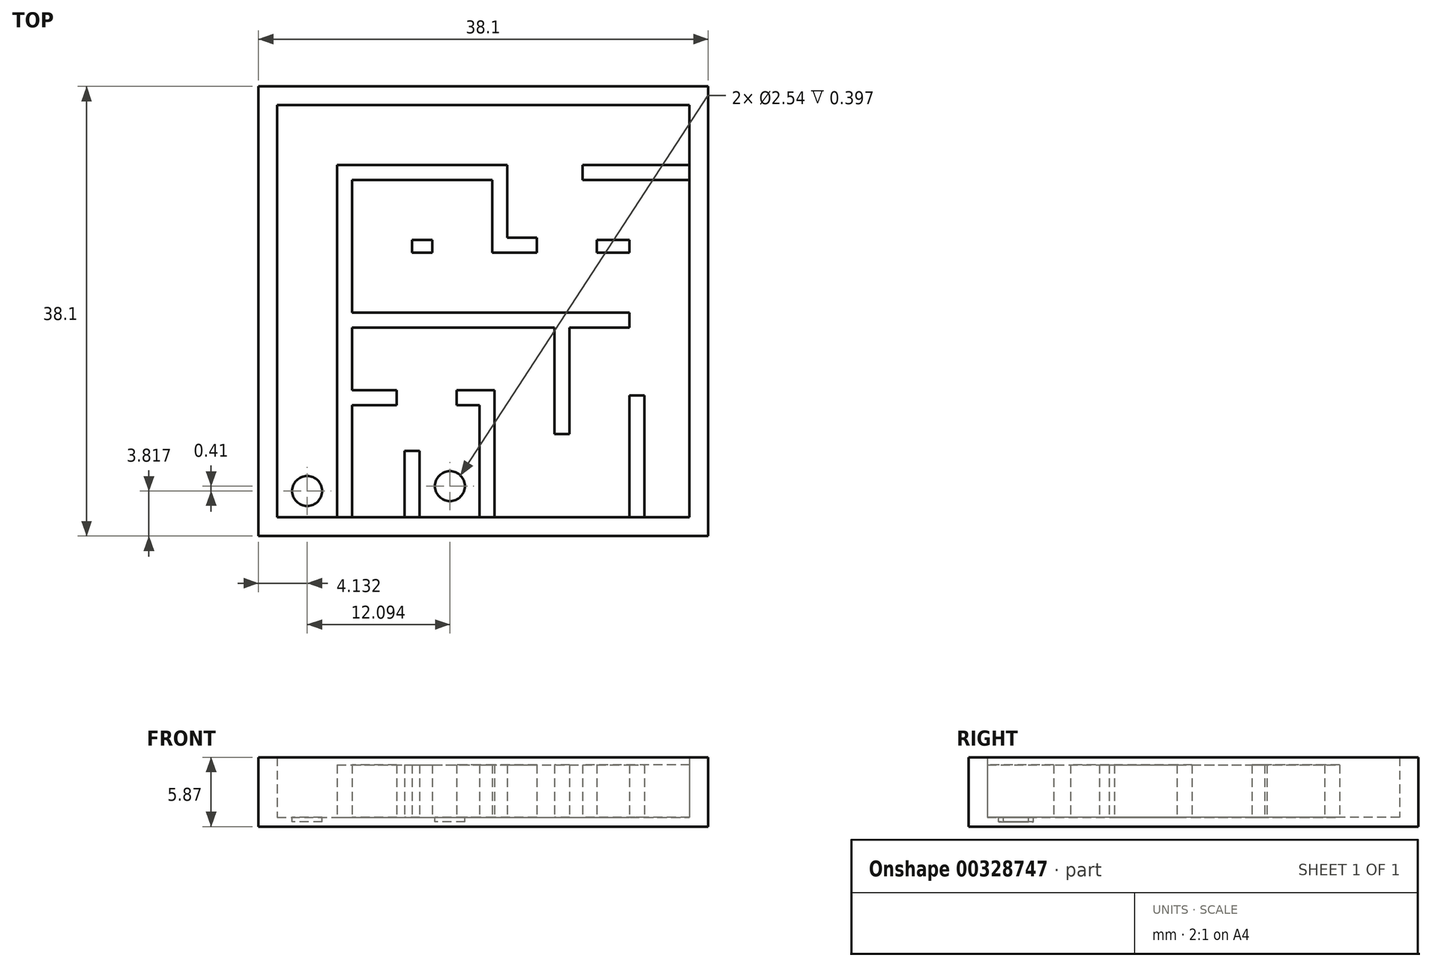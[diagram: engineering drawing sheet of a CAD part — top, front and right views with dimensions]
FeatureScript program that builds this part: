
annotation { "Feature Type Name" : "Feature", "Feature Type Description" : "" }
export const myFeature = defineFeature(function(context is Context, id is Id, definition is map)
    precondition{}
    {
        {
            var Q0;
            Q0=qCreatedBy(makeId("Top.planeOp"),FACE);
            var sketch = newSketch(context, id + "F0", { "sketchPlane" : qUnion([Q0])});
            skLineSegment(sketch, "E0.bottom", {"start": v(-18.59, 18.21) * mm, "end": v(19.51, 18.21) * mm});
            skLineSegment(sketch, "E0.top", {"start": v(-18.59, -19.89) * mm, "end": v(19.51, -19.89) * mm});
            skLineSegment(sketch, "E0.left", {"start": v(-18.59, 18.21) * mm, "end": v(-18.59, -19.89) * mm});
            skLineSegment(sketch, "E0.right", {"start": v(19.51, 18.21) * mm, "end": v(19.51, -19.89) * mm});
            skSolve(sketch);
        }
        {
            var Q0;
            Q0=makeQuery(id+"F0.imprint","IMPRINT",FACE,{"disambiguationData":[TD([[makeQuery(id+"F0.imprint","IMPRINT",EDGE,{"derivedFrom":sQuery(id+"F0.wireOp",EDGE,"E0.bottom")}),-1.0]])]});
            extrude(context, id + "F1", {"entities" : qUnion([Q0]), "depth" : 0.8 * mm});
        }
        {
            var Q0;
            Q0=makeQuery(id+"F1.opExtrude","CAP_FACE",FACE,{"disambiguationData":[OSD([sQuery(id+"F0.wireOp",EDGE,"E0.bottom"),sQuery(id+"F0.wireOp",EDGE,"E0.top"),sQuery(id+"F0.wireOp",EDGE,"E0.left"),sQuery(id+"F0.wireOp",EDGE,"E0.right")])],"isStart":false});
            var sketch = newSketch(context, id + "F2", { "sketchPlane" : qUnion([Q0])});
            skLineSegment(sketch, "E1.0", {"start": v(-17, 16.62) * mm, "end": v(17.93, 16.62) * mm});
            skLineSegment(sketch, "E1.1", {"start": v(-17, 16.62) * mm, "end": v(-17, -18.3) * mm});
            skLineSegment(sketch, "E1.2", {"start": v(-17, -18.3) * mm, "end": v(17.93, -18.3) * mm});
            skLineSegment(sketch, "E1.3", {"start": v(17.93, 16.62) * mm, "end": v(17.93, -18.3) * mm});
            skSolve(sketch);
        }
        {
            var Q0;
            Q0=makeQuery(id+"F2.imprint","IMPRINT",FACE,{"disambiguationData":[TD([[makeQuery(id+"F2.imprint","IMPRINT",EDGE,{"derivedFrom":sQuery(id+"F2.wireOp",EDGE,"E1.0")}),1.0]])]});
            extrude(context, id + "F3", {"entities" : qUnion([Q0]), "operationType" : NewBodyOperationType.ADD, "depth" : 5.08 * mm});
        }
        {
            var Q0;
            Q0=makeQuery(id+"F1.opExtrude","CAP_FACE",FACE,{"disambiguationData":[OSD([sQuery(id+"F0.wireOp",EDGE,"E0.bottom"),sQuery(id+"F0.wireOp",EDGE,"E0.top"),sQuery(id+"F0.wireOp",EDGE,"E0.left"),sQuery(id+"F0.wireOp",EDGE,"E0.right")])],"isStart":false});
            var sketch = newSketch(context, id + "F4", { "sketchPlane" : qUnion([Q0])});
            skLineSegment(sketch, "E2.bottom", {"start": v(-11.92, -18.3) * mm, "end": v(-10.65, -18.3) * mm});
            skLineSegment(sketch, "E2.top", {"start": v(-11.92, 11.54) * mm, "end": v(-10.65, 11.54) * mm});
            skLineSegment(sketch, "E2.left", {"start": v(-11.92, -18.3) * mm, "end": v(-11.92, 11.54) * mm});
            skLineSegment(sketch, "E2.right", {"start": v(-10.65, -18.3) * mm, "end": v(-10.65, -8.81) * mm});
            skLineSegment(sketch, "E3.bottom", {"start": v(-10.65, 11.54) * mm, "end": v(2.5, 11.54) * mm});
            skLineSegment(sketch, "E3.top", {"start": v(-10.65, 10.27) * mm, "end": v(1.22, 10.27) * mm});
            skLineSegment(sketch, "E3.right", {"start": v(2.5, 11.54) * mm, "end": v(2.5, 10.27) * mm});
            skLineSegment(sketch, "E4.bottom", {"start": v(17.93, 11.54) * mm, "end": v(8.87, 11.54) * mm});
            skLineSegment(sketch, "E4.top", {"start": v(17.93, 10.27) * mm, "end": v(8.87, 10.27) * mm});
            skLineSegment(sketch, "E4.left", {"start": v(17.93, 11.54) * mm, "end": v(17.93, 10.27) * mm});
            skLineSegment(sketch, "E4.right", {"start": v(8.87, 11.54) * mm, "end": v(8.87, 10.27) * mm});
            skLineSegment(sketch, "E5.top", {"start": v(2.5, 4.12) * mm, "end": v(1.22, 4.12) * mm});
            skLineSegment(sketch, "E5.left", {"start": v(2.5, 10.27) * mm, "end": v(2.5, 5.4) * mm});
            skLineSegment(sketch, "E5.right", {"start": v(1.22, 10.27) * mm, "end": v(1.22, 4.12) * mm});
            skLineSegment(sketch, "E6.bottom", {"start": v(-10.65, -0.96) * mm, "end": v(12.85, -0.96) * mm});
            skLineSegment(sketch, "E6.top", {"start": v(-10.65, -2.23) * mm, "end": v(6.5, -2.23) * mm});
            skLineSegment(sketch, "E6.right", {"start": v(12.85, -0.96) * mm, "end": v(12.85, -2.23) * mm});
            skLineSegment(sketch, "E7.trimOffspring", {"start": v(-10.65, -0.96) * mm, "end": v(-10.65, 10.27) * mm});
            skLineSegment(sketch, "E8.bottom", {"start": v(2.5, 4.12) * mm, "end": v(5, 4.12) * mm});
            skLineSegment(sketch, "E8.top", {"start": v(2.5, 5.4) * mm, "end": v(5, 5.4) * mm});
            skLineSegment(sketch, "E8.right", {"start": v(5, 4.12) * mm, "end": v(5, 5.4) * mm});
            skLineSegment(sketch, "E9.bottom", {"start": v(14.12, -18.3) * mm, "end": v(12.85, -18.3) * mm});
            skLineSegment(sketch, "E9.top", {"start": v(14.12, -8) * mm, "end": v(12.85, -8) * mm});
            skLineSegment(sketch, "E9.left", {"start": v(14.12, -18.3) * mm, "end": v(14.12, -8) * mm});
            skLineSegment(sketch, "E9.right", {"start": v(12.85, -18.3) * mm, "end": v(12.85, -8) * mm});
            skLineSegment(sketch, "E10", {"start": v(-11.92, -18.3) * mm, "end": v(-17, -18.3) * mm});
            skCircle(sketch, "E11", {"center": v(-14.46, -16.07) * mm, "radius": 1.27 * mm});
            skPoint(sketch, "E11.centerSnap0", {"position": v(-14.46, -18.3) * mm});
            skLineSegment(sketch, "E12.bottom", {"start": v(10.08, 5.2) * mm, "end": v(12.85, 5.2) * mm});
            skLineSegment(sketch, "E12.top", {"start": v(10.08, 4.12) * mm, "end": v(12.85, 4.12) * mm});
            skLineSegment(sketch, "E12.left", {"start": v(10.08, 5.2) * mm, "end": v(10.08, 4.12) * mm});
            skLineSegment(sketch, "E12.right", {"start": v(12.85, 5.2) * mm, "end": v(12.85, 4.12) * mm});
            skLineSegment(sketch, "E13.top", {"start": v(7.77, -11.26) * mm, "end": v(6.5, -11.26) * mm});
            skLineSegment(sketch, "E13.left", {"start": v(7.77, -2.23) * mm, "end": v(7.77, -11.26) * mm});
            skLineSegment(sketch, "E13.right", {"start": v(6.5, -2.23) * mm, "end": v(6.5, -11.26) * mm});
            skLineSegment(sketch, "E14.bottom", {"start": v(1.42, -18.3) * mm, "end": v(0.15, -18.3) * mm});
            skLineSegment(sketch, "E14.top", {"start": v(1.42, -7.54) * mm, "end": v(0.15, -7.54) * mm});
            skLineSegment(sketch, "E14.left", {"start": v(0.15, -18.3) * mm, "end": v(0.15, -8.81) * mm});
            skLineSegment(sketch, "E14.right", {"start": v(1.42, -18.3) * mm, "end": v(1.42, -7.54) * mm});
            skLineSegment(sketch, "E15.trimOffspring", {"start": v(7.77, -2.23) * mm, "end": v(12.85, -2.23) * mm});
            skLineSegment(sketch, "E16.bottom", {"start": v(-5.57, 5.2) * mm, "end": v(-3.86, 5.2) * mm});
            skLineSegment(sketch, "E16.top", {"start": v(-5.57, 4.12) * mm, "end": v(-3.86, 4.12) * mm});
            skLineSegment(sketch, "E16.left", {"start": v(-5.57, 5.2) * mm, "end": v(-5.57, 4.12) * mm});
            skLineSegment(sketch, "E16.right", {"start": v(-3.86, 5.2) * mm, "end": v(-3.86, 4.12) * mm});
            skLineSegment(sketch, "E17.bottom", {"start": v(0.15, -7.54) * mm, "end": v(-1.8, -7.54) * mm});
            skLineSegment(sketch, "E17.top", {"start": v(0.15, -8.81) * mm, "end": v(-1.8, -8.81) * mm});
            skLineSegment(sketch, "E17.right", {"start": v(-1.8, -7.54) * mm, "end": v(-1.8, -8.81) * mm});
            skLineSegment(sketch, "E18.bottom", {"start": v(-6.88, -8.81) * mm, "end": v(-10.65, -8.81) * mm});
            skLineSegment(sketch, "E18.top", {"start": v(-6.88, -7.54) * mm, "end": v(-10.65, -7.54) * mm});
            skLineSegment(sketch, "E18.left", {"start": v(-6.88, -8.81) * mm, "end": v(-6.88, -7.54) * mm});
            skPoint(sketch, "E19.firstSnap0", {"position": v(-0.82, -7.54) * mm});
            skLineSegment(sketch, "E20.bottom", {"start": v(-4.93, -12.7) * mm, "end": v(-6.2, -12.7) * mm});
            skLineSegment(sketch, "E20.top", {"start": v(-4.93, -18.3) * mm, "end": v(-6.2, -18.3) * mm});
            skLineSegment(sketch, "E20.left", {"start": v(-4.93, -12.7) * mm, "end": v(-4.93, -18.3) * mm});
            skLineSegment(sketch, "E20.right", {"start": v(-6.2, -12.7) * mm, "end": v(-6.2, -18.3) * mm});
            skLineSegment(sketch, "E21.top", {"start": v(-8.85, -18.3) * mm, "end": v(1.48, -18.3) * mm});
            skLineSegment(sketch, "E22", {"start": v(-6.2, -18.3) * mm, "end": v(1.48, -18.3) * mm});
            skCircle(sketch, "E23", {"center": v(-2.36, -15.66) * mm, "radius": 1.27 * mm});
            skPoint(sketch, "E23.centerSnap0", {"position": v(-2.36, -18.3) * mm});
            skLineSegment(sketch, "E24.trimOffspring", {"start": v(-10.65, -7.54) * mm, "end": v(-10.65, -2.23) * mm});
            skSolve(sketch);
        }
        {
            var Q0;
            Q0=makeQuery(id+"F4.imprint","IMPRINT",FACE,{"disambiguationData":[TD([[makeQuery(id+"F4.imprint","IMPRINT",EDGE,{"derivedFrom":sQuery(id+"F4.wireOp",EDGE,"E2.bottom")}),1.0]])]});
            var Q1;
            Q1=makeQuery(id+"F4.imprint","IMPRINT",FACE,{"disambiguationData":[TD([[makeQuery(id+"F4.imprint","IMPRINT",EDGE,{"derivedFrom":sQuery(id+"F4.wireOp",EDGE,"E4.bottom")}),1.0]])]});
            extrude(context, id + "F5", {"entities" : qUnion([Q0, Q1]), "operationType" : NewBodyOperationType.ADD, "depth" : 4.44 * mm});
        }
        {
            var Q0;
            Q0 = qSketchRegion(id + "F4", true);
            extrude(context, id + "F6", {"entities" : qUnion([Q0]), "operationType" : NewBodyOperationType.ADD, "depth" : 4.44 * mm});
        }
        {
            var Q0;
            Q0=makeQuery(id+"F6.opExtrude","CAP_FACE",FACE,{"disambiguationData":[OSD([sQuery(id+"F4.wireOp",EDGE,"E11")])],"isStart":false});
            var Q1;
            Q1=makeQuery(id+"F6.opExtrude","CAP_FACE",FACE,{"disambiguationData":[OSD([sQuery(id+"F4.wireOp",EDGE,"E23")])],"isStart":false});
            extrude(context, id + "F7", {"entities" : qUnion([Q0, Q1]), "operationType" : NewBodyOperationType.REMOVE, "oppositeDirection" : true, "depth" : 4.44 * mm});
        }
        {
            var Q0;
            Q0=makeQuery(id+"F4.imprint","IMPRINT",FACE,{"disambiguationData":[TD([[makeQuery(id+"F4.imprint","IMPRINT",EDGE,{"derivedFrom":sQuery(id+"F4.wireOp",EDGE,"E11")}),1.0]])]});
            var Q1;
            Q1=makeQuery(id+"F4.imprint","IMPRINT",FACE,{"disambiguationData":[TD([[makeQuery(id+"F4.imprint","IMPRINT",EDGE,{"derivedFrom":sQuery(id+"F4.wireOp",EDGE,"E23")}),1.0]])]});
            extrude(context, id + "F8", {"entities" : qUnion([Q0, Q1]), "operationType" : NewBodyOperationType.REMOVE, "oppositeDirection" : true, "depth" : 0.4 * mm});
        }
    });
